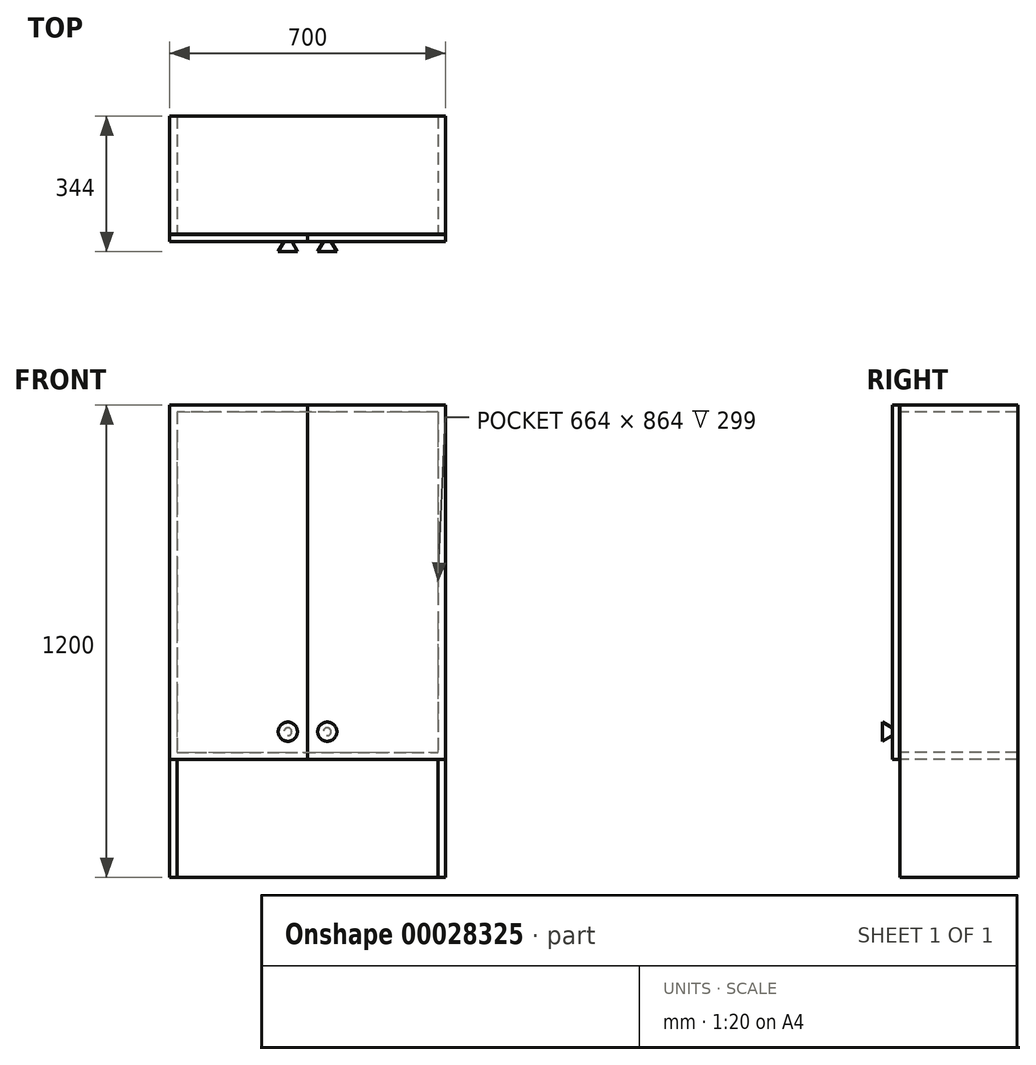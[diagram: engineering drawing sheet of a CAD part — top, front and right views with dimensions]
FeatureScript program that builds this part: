
annotation { "Feature Type Name" : "Feature", "Feature Type Description" : "" }
export const myFeature = defineFeature(function(context is Context, id is Id, definition is map)
    precondition{}
    {
        {
            var Q0;
            Q0=qCreatedBy(makeId("Top.planeOp"),FACE);
            var sketch = newSketch(context, id + "F0", { "sketchPlane" : qUnion([Q0])});
            skLineSegment(sketch, "E0.bottom", {"start": v(0, 0) * mm, "end": v(-350, 0) * mm});
            skLineSegment(sketch, "E0.top", {"start": v(0, -300) * mm, "end": v(-350, -300) * mm});
            skLineSegment(sketch, "E0.left", {"start": v(0, 0) * mm, "end": v(0, -300) * mm});
            skLineSegment(sketch, "E0.right", {"start": v(-350, 0) * mm, "end": v(-350, -300) * mm});
            skSolve(sketch);
        }
        {
            var Q0;
            Q0=makeQuery(id+"F0.imprint","IMPRINT",FACE,{"disambiguationData":[TD([[makeQuery(id+"F0.imprint","IMPRINT",EDGE,{"derivedFrom":sQuery(id+"F0.wireOp",EDGE,"E0.bottom")}),1.0]])]});
            extrude(context, id + "F1", {"entities" : qUnion([Q0]), "depth" : 18 * mm});
        }
        {
            var Q0;
            Q0=makeQuery(id+"F1.opExtrude","CAP_FACE",FACE,{"disambiguationData":[OSD([sQuery(id+"F0.wireOp",EDGE,"E0.bottom"),sQuery(id+"F0.wireOp",EDGE,"E0.top"),sQuery(id+"F0.wireOp",EDGE,"E0.left"),sQuery(id+"F0.wireOp",EDGE,"E0.right")])],"isStart":false});
            var sketch = newSketch(context, id + "F2", { "sketchPlane" : qUnion([Q0])});
            skLineSegment(sketch, "E1.bottom", {"start": v(-350, 0) * mm, "end": v(-332, 0) * mm});
            skLineSegment(sketch, "E1.top", {"start": v(-350, -300) * mm, "end": v(-332, -300) * mm});
            skLineSegment(sketch, "E1.left", {"start": v(-350, 0) * mm, "end": v(-350, -300) * mm});
            skLineSegment(sketch, "E1.right", {"start": v(-332, 0) * mm, "end": v(-332, -300) * mm});
            skLineSegment(sketch, "E2.bottom", {"start": v(-332, 0) * mm, "end": v(0, 0) * mm});
            skLineSegment(sketch, "E2.top", {"start": v(-332, -1) * mm, "end": v(0, -1) * mm});
            skLineSegment(sketch, "E2.left", {"start": v(-332, 0) * mm, "end": v(-332, -1) * mm});
            skLineSegment(sketch, "E2.right", {"start": v(0, 0) * mm, "end": v(0, -1) * mm});
            skSolve(sketch);
        }
        {
            var Q0;
            Q0 = qSketchRegion(id + "F2", true);
            extrude(context, id + "F3", {"entities" : qUnion([Q0]), "operationType" : NewBodyOperationType.ADD, "depth" : 864 * mm});
        }
        {
            var Q0;
            Q0=makeQuery(id+"F3.opExtrude","CAP_FACE",FACE,{"disambiguationData":[OSD([sQuery(id+"F2.wireOp",EDGE,"E1.bottom"),sQuery(id+"F2.wireOp",EDGE,"E1.top"),sQuery(id+"F2.wireOp",EDGE,"E1.left"),sQuery(id+"F2.wireOp",EDGE,"E1.right"),sQuery(id+"F2.wireOp",EDGE,"E2.bottom"),sQuery(id+"F2.wireOp",EDGE,"E2.top"),sQuery(id+"F2.wireOp",EDGE,"E2.right")])],"isStart":false});
            var sketch = newSketch(context, id + "F4", { "sketchPlane" : qUnion([Q0])});
            skLineSegment(sketch, "E3.bottom", {"start": v(-350, 0) * mm, "end": v(0, 0) * mm});
            skLineSegment(sketch, "E3.top", {"start": v(-350, -300) * mm, "end": v(0, -300) * mm});
            skLineSegment(sketch, "E3.left", {"start": v(-350, 0) * mm, "end": v(-350, -300) * mm});
            skLineSegment(sketch, "E3.right", {"start": v(0, 0) * mm, "end": v(0, -300) * mm});
            skSolve(sketch);
        }
        {
            var Q0;
            Q0 = qSketchRegion(id + "F4", true);
            extrude(context, id + "F5", {"entities" : qUnion([Q0]), "operationType" : NewBodyOperationType.ADD, "depth" : 18 * mm});
        }
        {
            var Q0;
            Q0 = qSketchRegion(id + "F2", true);
            extrude(context, id + "F6", {"entities" : qUnion([Q0]), "operationType" : NewBodyOperationType.ADD, "oppositeDirection" : true, "depth" : 318 * mm});
        }
        {
            var Q0;
            Q0=makeQuery(id+"F1.opExtrude","SWEPT_BODY",BODY,{"disambiguationData":[OSD([sQuery(id+"F0.wireOp",EDGE,"E0.bottom"),sQuery(id+"F0.wireOp",EDGE,"E0.top"),sQuery(id+"F0.wireOp",EDGE,"E0.left"),sQuery(id+"F0.wireOp",EDGE,"E0.right")])]});
            var Q1;
            Q1=qCreatedBy(makeId("Right.planeOp"),FACE);
            mirror(context, id + "F7", {"operationType" : NewBodyOperationType.ADD, "entities" : qUnion([Q0]), "mirrorPlane" : qUnion([Q1])});
        }
        {
            var Q0;
            {var subQ0=makeQuery(id+"Fgfnsvy72F9b6Xe_2.opBoolean","MERGE",FACE,{"derivedFrom":[makeQuery(id+"F3.boolean.opBoolean","MERGE",FACE,{"derivedFrom":[makeQuery(id+"F1.opExtrude","SWEPT_FACE",FACE,{"disambiguationData":[OSD([sQuery(id+"F0.wireOp",EDGE,"E0.top")])]}),makeQuery(id+"F3.opExtrude","SWEPT_FACE",FACE,{"disambiguationData":[OSD([sQuery(id+"F2.wireOp",EDGE,"E1.top")])]})]}),makeQuery(id+"F9sv2vTZeiZ0ifi_1.opExtrude","SWEPT_FACE",FACE,{"disambiguationData":[OSD([sQuery(id+"F4.wireOp",EDGE,"E3.top")])]})]});Q0=makeQuery(id+"F7.boolean.opBoolean","MERGE",FACE,{"derivedFrom":[subQ0,makeQuery(id+"F7.opPattern","COPY",FACE,{"derivedFrom":subQ0,"instanceName":"1"})]});}
            cPlane(context, id + "F8", {"entities" : qUnion([Q0]), "cplaneType" : CPlaneType.OFFSET, "offset" : 1 * mm, "width" : 150 * mm, "height" : 150 * mm});
        }
        {
            var Q0;
            Q0=qCreatedBy(id+"F8.planeOp",FACE);
            var sketch = newSketch(context, id + "F9", { "sketchPlane" : qUnion([Q0])});
            skPoint(sketch, "E4.0", {"position": v(0, 0) * mm});
            skLineSegment(sketch, "E5.bottom", {"start": v(-350, 900) * mm, "end": v(0, 900) * mm});
            skLineSegment(sketch, "E5.top", {"start": v(-350, 0) * mm, "end": v(0, 0) * mm});
            skLineSegment(sketch, "E5.left", {"start": v(-350, 900) * mm, "end": v(-350, 0) * mm});
            skLineSegment(sketch, "E5.right", {"start": v(0, 900) * mm, "end": v(0, 0) * mm});
            skPoint(sketch, "E6.0", {"position": v(-350, 900) * mm});
            skSolve(sketch);
        }
        {
            var Q0;
            Q0 = qSketchRegion(id + "F9", true);
            extrude(context, id + "F10", {"entities" : qUnion([Q0]), "depth" : 18 * mm});
        }
        {
            var Q0;
            Q0=makeQuery(id+"F10.opExtrude","CAP_FACE",FACE,{"disambiguationData":[OSD([sQuery(id+"F9.wireOp",EDGE,"E5.bottom"),sQuery(id+"F9.wireOp",EDGE,"E5.top"),sQuery(id+"F9.wireOp",EDGE,"E5.left"),sQuery(id+"F9.wireOp",EDGE,"E5.right")])],"isStart":false});
            var sketch = newSketch(context, id + "F11", { "sketchPlane" : qUnion([Q0])});
            skCircle(sketch, "E7", {"center": v(-50, 70) * mm, "radius": 10 * mm});
            skSolve(sketch);
        }
        {
            var Q0;
            Q0 = qSketchRegion(id + "F11", true);
            extrude(context, id + "F12", {"entities" : qUnion([Q0]), "operationType" : NewBodyOperationType.ADD, "depth" : 25 * mm, "hasDraft" : true, "draftAngle" : 30 * degree});
        }
        {
            var Q0;
            Q0=makeQuery(id+"F10.opExtrude","SWEPT_BODY",BODY,{"disambiguationData":[OSD([sQuery(id+"F9.wireOp",EDGE,"E5.bottom"),sQuery(id+"F9.wireOp",EDGE,"E5.top"),sQuery(id+"F9.wireOp",EDGE,"E5.left"),sQuery(id+"F9.wireOp",EDGE,"E5.right")])]});
            var Q1;
            Q1=qCreatedBy(makeId("Right.planeOp"),FACE);
            mirror(context, id + "F13", {"entities" : qUnion([Q0]), "mirrorPlane" : qUnion([Q1])});
        }
    });
